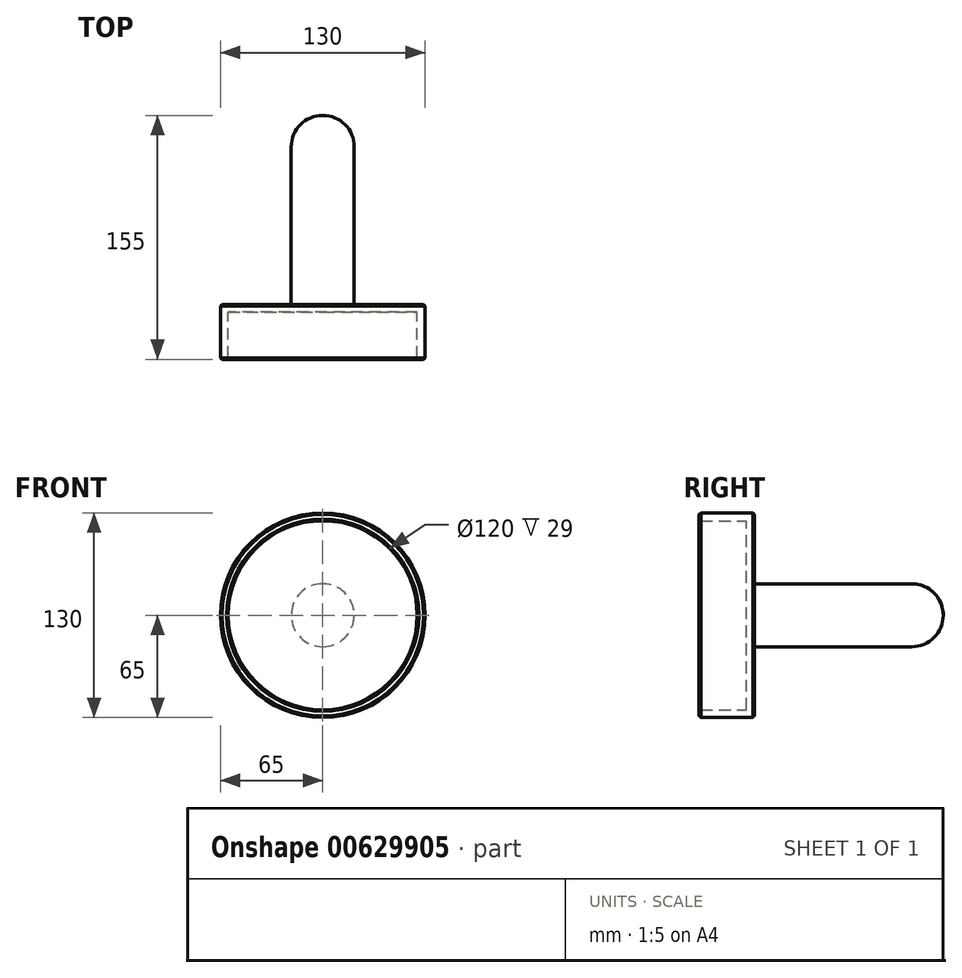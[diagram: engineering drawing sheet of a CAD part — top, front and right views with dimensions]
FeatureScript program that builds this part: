
annotation { "Feature Type Name" : "Feature", "Feature Type Description" : "" }
export const myFeature = defineFeature(function(context is Context, id is Id, definition is map)
    precondition{}
    {
        {
            var Q0;
            Q0=qCreatedBy(makeId("Front.planeOp"),FACE);
            var sketch = newSketch(context, id + "F0", { "sketchPlane" : qUnion([Q0])});
            skCircle(sketch, "E0", {"center": v(0, 0) * mm, "radius": 65 * mm});
            skSolve(sketch);
        }
        {
            var Q0;
            Q0 = qSketchRegion(id + "F0", true);
            extrude(context, id + "F1", {"entities" : qUnion([Q0]), "oppositeDirection" : true, "depth" : 5 * mm, "offsetDistance" : 25 * mm});
        }
        {
            var Q0;
            Q0=makeQuery(id+"F1.opExtrude","CAP_FACE",FACE,{"disambiguationData":[OSD([sQuery(id+"F0.wireOp",EDGE,"E0")])],"isStart":true});
            var sketch = newSketch(context, id + "F2", { "sketchPlane" : qUnion([Q0])});
            skCircle(sketch, "E1", {"center": v(0, 0) * mm, "radius": 60 * mm});
            skSolve(sketch);
        }
        {
            var Q0;
            Q0=makeQuery(id+"F2.imprint","IMPRINT",FACE,{"disambiguationData":[TD([[makeQuery(id+"F2.imprint","IMPRINT",EDGE,{"derivedFrom":sQuery(id+"F2.wireOp",EDGE,"E1")}),-1.0]])]});
            extrude(context, id + "F3", {"entities" : qUnion([Q0]), "operationType" : NewBodyOperationType.ADD, "depth" : 30 * mm, "offsetDistance" : 25 * mm});
        }
        {
            var Q0;
            Q0=makeQuery(id+"F1.opExtrude","CAP_FACE",FACE,{"disambiguationData":[OSD([sQuery(id+"F0.wireOp",EDGE,"E0")])],"isStart":false});
            var sketch = newSketch(context, id + "F4", { "sketchPlane" : qUnion([Q0])});
            skCircle(sketch, "E2", {"center": v(0, 0) * mm, "radius": 20 * mm});
            skSolve(sketch);
        }
        {
            var Q0;
            Q0=makeQuery(id+"F4.imprint","IMPRINT",FACE,{"disambiguationData":[TD([[makeQuery(id+"F4.imprint","IMPRINT",EDGE,{"derivedFrom":sQuery(id+"F4.wireOp",EDGE,"E2")}),1.0]])]});
            extrude(context, id + "F5", {"entities" : qUnion([Q0]), "operationType" : NewBodyOperationType.ADD, "depth" : 120 * mm, "offsetDistance" : 25 * mm});
        }
        {
            var Q0;
            Q0=makeQuery(id+"F5.opExtrude","CAP_EDGE",EDGE,{"disambiguationData":[OSD([sQuery(id+"F4.wireOp",EDGE,"E2")])],"isStart":false});
            fillet(context, id + "F6", {"entities" : qUnion([Q0]), "radius" : 20 * mm, "tangentPropagation" : true, "allowEdgeOverflow" : false});
        }
        {
            var Q0;
            Q0=makeQuery(id+"F1.opExtrude","CAP_EDGE",EDGE,{"disambiguationData":[OSD([sQuery(id+"F0.wireOp",EDGE,"E0")])],"isStart":false});
            var Q1;
            Q1=makeQuery(id+"F3.opExtrude","CAP_EDGE",EDGE,{"disambiguationData":[OSD([sQuery(id+"F0.wireOp",EDGE,"E0")])],"isStart":false});
            var Q2;
            Q2=makeQuery(id+"F3.opExtrude","CAP_EDGE",EDGE,{"disambiguationData":[OSD([sQuery(id+"F2.wireOp",EDGE,"E1")])],"isStart":false});
            chamfer(context, id + "F7", {"entities" : qUnion([Q0, Q1, Q2]), "width" : 1 * mm, "tangentPropagation" : true});
        }
    });
